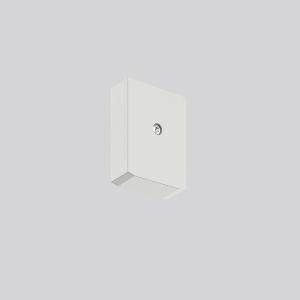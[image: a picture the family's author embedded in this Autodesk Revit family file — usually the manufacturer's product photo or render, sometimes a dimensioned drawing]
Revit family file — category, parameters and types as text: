
# Revit family: linedo_endkappe_b_f_982700_009_3cd6
name_source: partatom
category: Lighting Fixtures
units: mm (PartAtom-declared; Revit-internal decimal feet)

## family parameters
Cut with Voids When Loaded = No
Host = Face
Light Source = No
Part Type = Normal
Room Calculation Point = No
Round Connector Dimension = Use Diameter
Shared = No

## types (1)
- LINEDO_Endkappe_B_F
    Apparent Load = 0 VA
    Default Elevation = 1800 mm
    Description = End cap low profile for LINEDO plug. Plastic end cap to cover the LINEDO plug system at the end of the line. Fastening by TX20 screw. Installation accessories included.
Colour: grey
Length: 23 mm
Width: 58 mm
Height: 76 mm
Weight: 31 g
    Height = 76 mm
    Lamp = 0 x
    Length = 23 mm
    Luminous efficacy = 0 lm/W
    Manufacturer = RZB
    ModVariant = No
    Model = 982700.009
    Mounting Place = Ceiling
    Mounting Type = Surface mounted, Pendant
    Number of Poles = 1
    OnlyDefault = Yes
    Power Factor = 1
    Product Name = LINEDO_Endkappe_B_F
    Product group = Continuous line luminaire system Linedo IP 54
    ProductGroupID = 314
    Protection Class = Protection class
    Protection Degree = Degree of protection
    RLX_Detail_Level = 1
    RLX_Emergency_Light_Flux = 0 lm
    RLX_Emergency_Type = 0
    RLX_Emergency_Type_DB = No
    RlxData = <blob elided: 8505 chars, md5=c85110b0>
    Standby Power = 0 W
    System Light Flux = 0 lm
    System Power = 0 W
    Type Comments = Product without accessories
    Type Image = 982700.009.jpg
    URL = http://relux.com
    VarID = ---
    Voltage = 0 V
    Weight = 0.00 kg
    Width = 58 mm

## geometry (parser evidence)
native form markers: Sweep x8
no freeform markers — native parametric forms only
